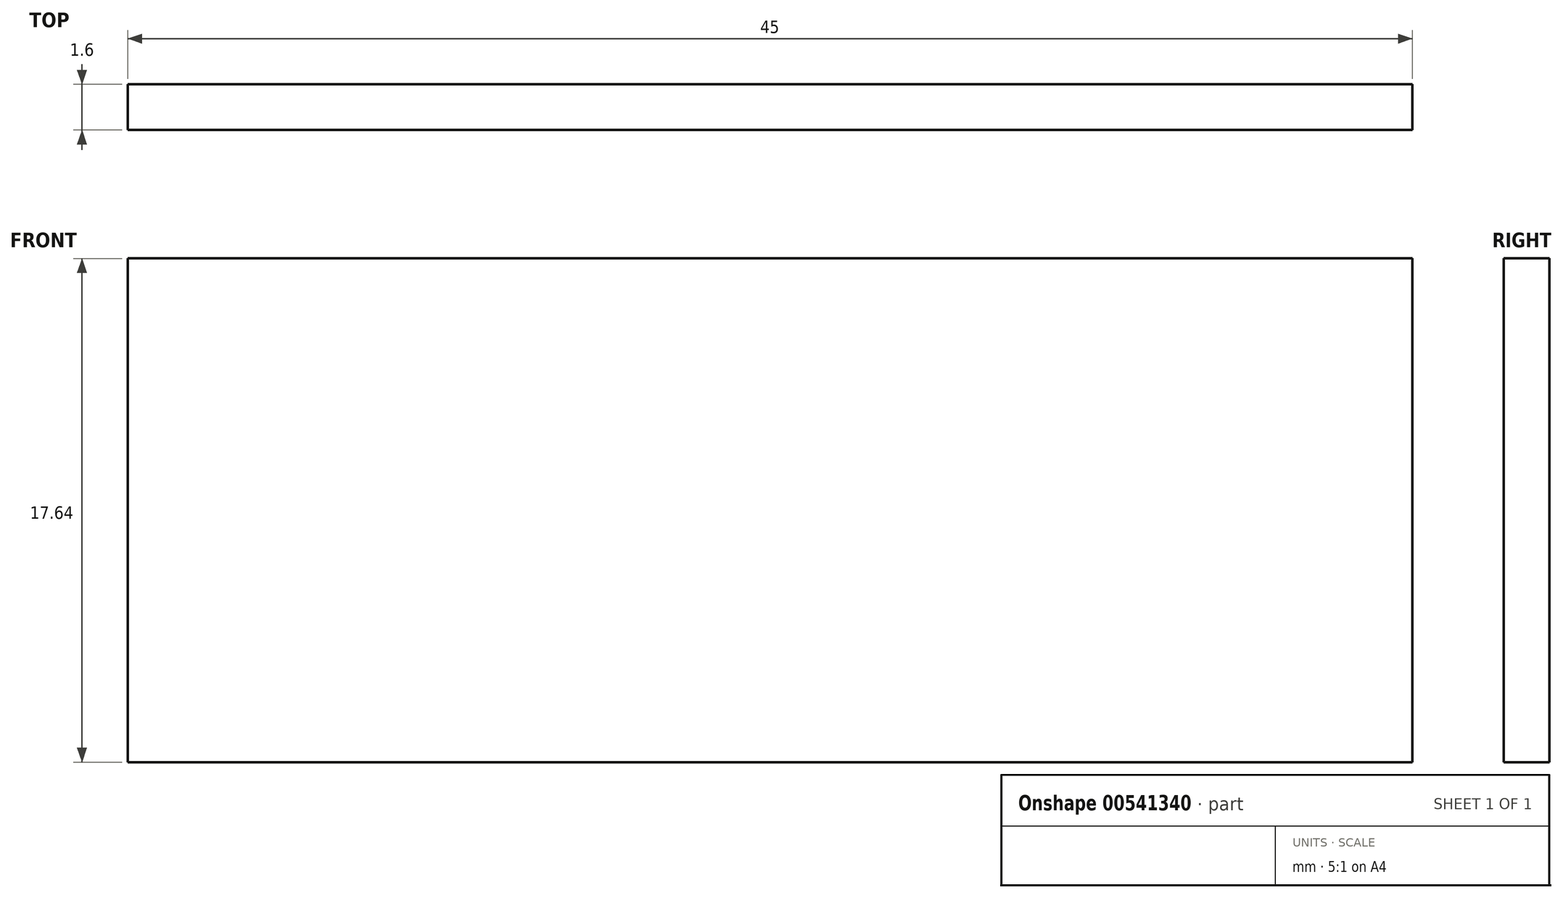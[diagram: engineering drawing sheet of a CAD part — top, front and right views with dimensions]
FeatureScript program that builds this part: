
annotation { "Feature Type Name" : "Feature", "Feature Type Description" : "" }
export const myFeature = defineFeature(function(context is Context, id is Id, definition is map)
    precondition{}
    {
        {
            var Q0;
            Q0=qCreatedBy(makeId("Front.planeOp"),FACE);
            var sketch = newSketch(context, id + "F0", { "sketchPlane" : qUnion([Q0])});
            skLineSegment(sketch, "E0.bottom", {"start": v(22.5, 8.82) * mm, "end": v(-22.5, 8.82) * mm});
            skLineSegment(sketch, "E0.top", {"start": v(22.5, -8.82) * mm, "end": v(-22.5, -8.82) * mm});
            skLineSegment(sketch, "E0.left", {"start": v(22.5, 8.82) * mm, "end": v(22.5, -8.82) * mm});
            skLineSegment(sketch, "E0.right", {"start": v(-22.5, 8.82) * mm, "end": v(-22.5, -8.82) * mm});
            skPoint(sketch, "E0.middle", {"position": v(0, 0) * mm});
            skSolve(sketch);
        }
        {
            var Q0;
            Q0 = qSketchRegion(id + "F0", true);
            extrude(context, id + "F1", {"entities" : qUnion([Q0]), "depth" : 1.6 * mm, "offsetDistance" : 25.4 * mm});
        }
    });
